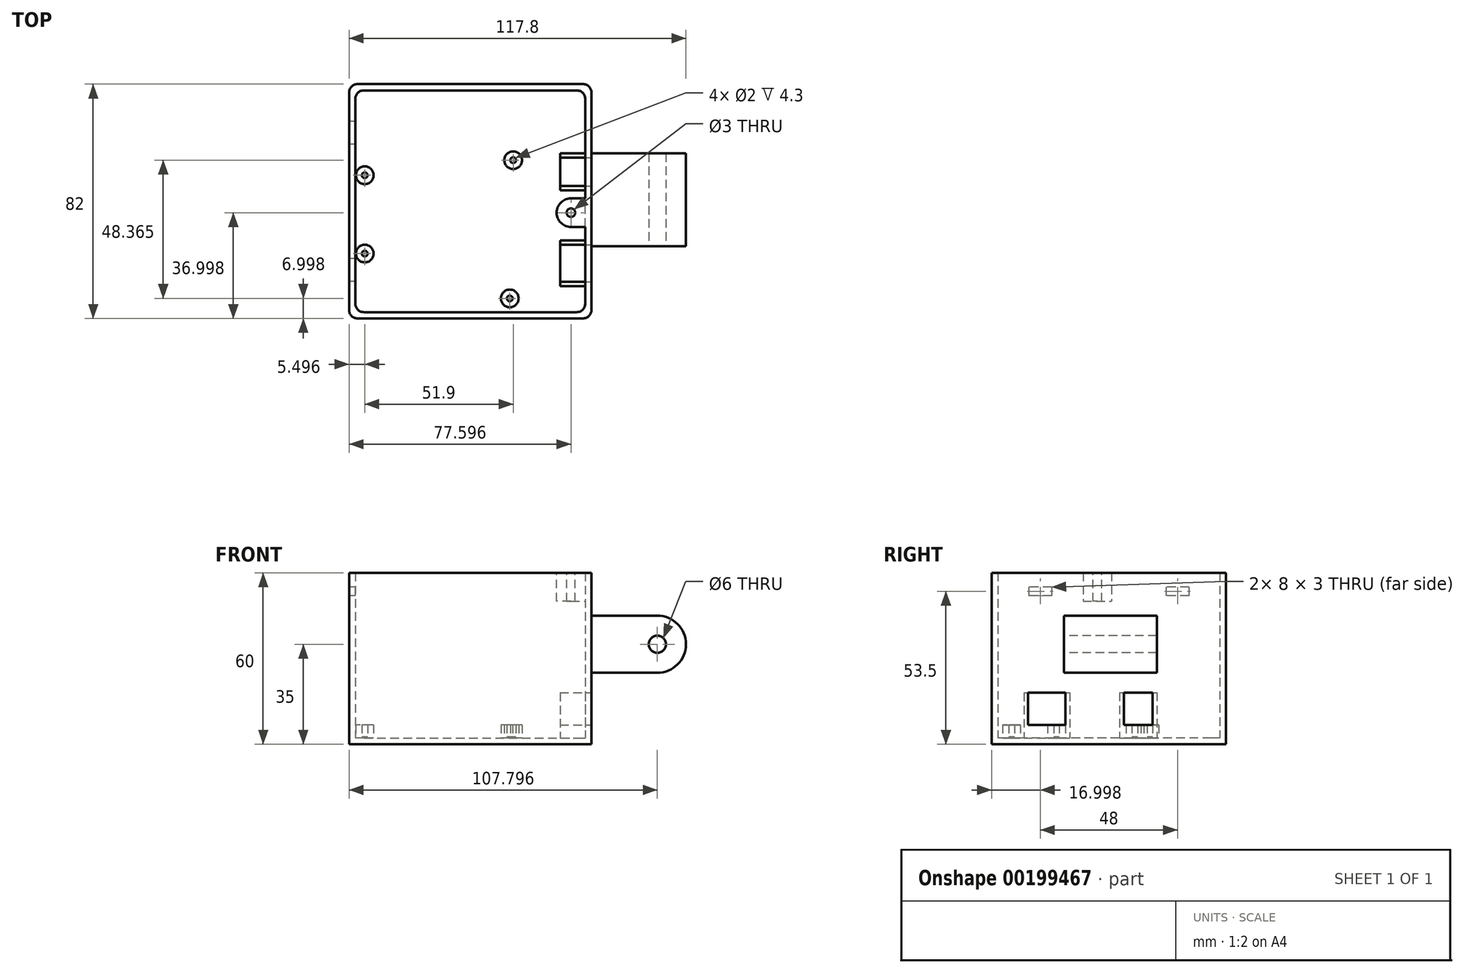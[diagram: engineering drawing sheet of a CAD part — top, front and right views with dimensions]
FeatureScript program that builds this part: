
annotation { "Feature Type Name" : "Feature", "Feature Type Description" : "" }
export const myFeature = defineFeature(function(context is Context, id is Id, definition is map)
    precondition{}
    {
        {
            var Q0;
            Q0=qCreatedBy(makeId("Top.planeOp"),FACE);
            var sketch = newSketch(context, id + "F0", { "sketchPlane" : qUnion([Q0])});
            skLineSegment(sketch, "E0.bottom", {"start": v(-75.5, 40.49) * mm, "end": v(9.3, 40.49) * mm});
            skLineSegment(sketch, "E0.top", {"start": v(-75.5, -41.51) * mm, "end": v(9.3, -41.51) * mm});
            skLineSegment(sketch, "E0.left", {"start": v(-75.5, 40.49) * mm, "end": v(-75.5, -41.51) * mm});
            skLineSegment(sketch, "E0.right", {"start": v(9.3, 40.49) * mm, "end": v(9.3, -41.51) * mm});
            skCircle(sketch, "E1", {"center": v(-70, 8.59) * mm, "radius": 3.1 * mm});
            skCircle(sketch, "E2", {"center": v(-70, -18.81) * mm, "radius": 3.1 * mm});
            skCircle(sketch, "E3", {"center": v(-19.3, -34.51) * mm, "radius": 3.1 * mm});
            skCircle(sketch, "E4", {"center": v(-18.1, 13.85) * mm, "radius": 3.1 * mm});
            skCircle(sketch, "E5", {"center": v(-70, 8.59) * mm, "radius": 1 * mm});
            skCircle(sketch, "E6", {"center": v(-18.1, 13.85) * mm, "radius": 1 * mm});
            skCircle(sketch, "E7", {"center": v(-70, -18.81) * mm, "radius": 1 * mm});
            skCircle(sketch, "E8", {"center": v(-19.3, -34.51) * mm, "radius": 1 * mm});
            skSolve(sketch);
        }
        {
            var Q0;
            Q0=makeQuery(id+"F0.imprint","IMPRINT",FACE,{"disambiguationData":[TD([[makeQuery(id+"F0.imprint","IMPRINT",EDGE,{"derivedFrom":sQuery(id+"F0.wireOp",EDGE,"E0.bottom")}),-1.0]])]});
            var Q1;
            Q1=makeQuery(id+"F0.imprint","IMPRINT",FACE,{"disambiguationData":[TD([[makeQuery(id+"F0.imprint","IMPRINT",EDGE,{"derivedFrom":sQuery(id+"F0.wireOp",EDGE,"E2")}),1.0]])]});
            var Q2;
            Q2=makeQuery(id+"F0.imprint","IMPRINT",FACE,{"disambiguationData":[TD([[makeQuery(id+"F0.imprint","IMPRINT",EDGE,{"derivedFrom":sQuery(id+"F0.wireOp",EDGE,"E1")}),1.0]])]});
            var Q3;
            Q3=makeQuery(id+"F0.imprint","IMPRINT",FACE,{"disambiguationData":[TD([[makeQuery(id+"F0.imprint","IMPRINT",EDGE,{"derivedFrom":sQuery(id+"F0.wireOp",EDGE,"E4")}),1.0]])]});
            var Q4;
            Q4=makeQuery(id+"F0.imprint","IMPRINT",FACE,{"disambiguationData":[TD([[makeQuery(id+"F0.imprint","IMPRINT",EDGE,{"derivedFrom":sQuery(id+"F0.wireOp",EDGE,"E3")}),1.0]])]});
            extrude(context, id + "F1", {"entities" : qUnion([Q0, Q1, Q2, Q3, Q4]), "depth" : 60 * mm});
        }
        {
            var Q0;
            Q0=makeQuery(id+"F1.opExtrude","SWEPT_FACE",FACE,{"disambiguationData":[OSD([sQuery(id+"F0.wireOp",EDGE,"E2")])]});
            var Q1;
            Q1=makeQuery(id+"F1.opExtrude","SWEPT_FACE",FACE,{"disambiguationData":[OSD([sQuery(id+"F0.wireOp",EDGE,"E1")])]});
            var Q2;
            Q2=makeQuery(id+"F1.opExtrude","SWEPT_FACE",FACE,{"disambiguationData":[OSD([sQuery(id+"F0.wireOp",EDGE,"E4")])]});
            var Q3;
            Q3=makeQuery(id+"F1.opExtrude","SWEPT_FACE",FACE,{"disambiguationData":[OSD([sQuery(id+"F0.wireOp",EDGE,"E3")])]});
            var Q4;
            Q4=makeQuery(id+"F1.opExtrude","SWEPT_FACE",FACE,{"disambiguationData":[OSD([sQuery(id+"F0.wireOp",EDGE,"E7")])]});
            var Q5;
            Q5=makeQuery(id+"F1.opExtrude","SWEPT_FACE",FACE,{"disambiguationData":[OSD([sQuery(id+"F0.wireOp",EDGE,"E5")])]});
            var Q6;
            Q6=makeQuery(id+"F1.opExtrude","SWEPT_FACE",FACE,{"disambiguationData":[OSD([sQuery(id+"F0.wireOp",EDGE,"E8")])]});
            var Q7;
            Q7=makeQuery(id+"F1.opExtrude","SWEPT_FACE",FACE,{"disambiguationData":[OSD([sQuery(id+"F0.wireOp",EDGE,"E6")])]});
            var Q8;
            Q8=makeQuery(id+"F1.opExtrude","CAP_FACE",FACE,{"disambiguationData":[OSD([sQuery(id+"F0.wireOp",EDGE,"E0.bottom"),sQuery(id+"F0.wireOp",EDGE,"E0.left"),sQuery(id+"F0.wireOp",EDGE,"7W9O8lOB-wSMZ-6HX8-2Pzd-baJFNFpb0Sld")])],"isStart":false});
            var Q9;
            Q9=makeQuery(id+"F1.opExtrude","CAP_FACE",FACE,{"disambiguationData":[OSD([sQuery(id+"F0.wireOp",EDGE,"E0.bottom"),sQuery(id+"F0.wireOp",EDGE,"E0.right"),sQuery(id+"F0.wireOp",EDGE,"6wA7PAN0-a5WZ-xzTv-JZU7-1fsM9sgV2JZ6")])],"isStart":false});
            var Q10;
            Q10=makeQuery(id+"F1.opExtrude","SWEPT_FACE",FACE,{"disambiguationData":[OSD([sQuery(id+"F0.wireOp",EDGE,"u36fmcnV-SRn1-kItR-ujeD-uHerwh8gpMvl")])]});
            shell(context, id + "F2", {"entities" : qUnion([Q0, Q1, Q2, Q3, Q4, Q5, Q6, Q7, Q8, Q9, Q10]), "thickness" : 2.2 * mm});
        }
        {
            var Q0;
            Q0=makeQuery(id+"F1.opExtrude","SWEPT_FACE",FACE,{"disambiguationData":[OSD([sQuery(id+"F0.wireOp",EDGE,"E0.right")])]});
            var sketch = newSketch(context, id + "F3", { "sketchPlane" : qUnion([Q0])});
            skLineSegment(sketch, "E9.bottom", {"start": v(-28.71, 18.1) * mm, "end": v(-15.71, 18.1) * mm});
            skLineSegment(sketch, "E9.top", {"start": v(-28.71, 6.8) * mm, "end": v(-15.71, 6.8) * mm});
            skLineSegment(sketch, "E9.left", {"start": v(-28.71, 18.1) * mm, "end": v(-28.71, 6.8) * mm});
            skLineSegment(sketch, "E9.right", {"start": v(-15.71, 18.1) * mm, "end": v(-15.71, 6.8) * mm});
            skLineSegment(sketch, "E10.bottom", {"start": v(4.79, 18.1) * mm, "end": v(14.79, 18.1) * mm});
            skLineSegment(sketch, "E10.top", {"start": v(4.79, 6.8) * mm, "end": v(14.79, 6.8) * mm});
            skLineSegment(sketch, "E10.left", {"start": v(4.79, 18.1) * mm, "end": v(4.79, 6.8) * mm});
            skLineSegment(sketch, "E10.right", {"start": v(14.79, 18.1) * mm, "end": v(14.79, 6.8) * mm});
            skLineSegment(sketch, "E11.bottom", {"start": v(-30.21, 18.04) * mm, "end": v(-14.21, 18.04) * mm});
            skLineSegment(sketch, "E11.top", {"start": v(-30.21, 0) * mm, "end": v(-14.21, 0) * mm});
            skLineSegment(sketch, "E11.left", {"start": v(-30.21, 18.04) * mm, "end": v(-30.21, 0) * mm});
            skLineSegment(sketch, "E11.right", {"start": v(-14.21, 18.04) * mm, "end": v(-14.21, 0) * mm});
            skLineSegment(sketch, "E12.bottom", {"start": v(3.29, 18.1) * mm, "end": v(16.29, 18.1) * mm});
            skLineSegment(sketch, "E12.top", {"start": v(3.29, 0) * mm, "end": v(16.29, 0) * mm});
            skLineSegment(sketch, "E12.left", {"start": v(3.29, 18.1) * mm, "end": v(3.29, 0) * mm});
            skLineSegment(sketch, "E12.right", {"start": v(16.29, 18.1) * mm, "end": v(16.29, 0) * mm});
            skSolve(sketch);
        }
        {
            var Q0;
            {var subQ1=sQuery(id+"F3.wireOp",EDGE,"E9.top");Q0=makeQuery(id+"F3.imprint","IMPRINT",FACE,{"disambiguationData":[TD([[makeQuery(id+"F3.imprint","IMPRINT",EDGE,{"derivedFrom":subQ1}),-1.0]])]});}
            var Q1;
            Q1=makeQuery(id+"F3.imprint","IMPRINT",FACE,{"disambiguationData":[TD([[makeQuery(id+"F3.imprint","IMPRINT",EDGE,{"derivedFrom":sQuery(id+"F3.wireOp",EDGE,"E10.top")}),-1.0]])]});
            extrude(context, id + "F4", {"entities" : qUnion([Q0, Q1]), "operationType" : NewBodyOperationType.ADD, "oppositeDirection" : true, "depth" : 11 * mm});
        }
        {
            var Q0;
            {var subQ0=sQuery(id+"F3.wireOp",EDGE,"E9.top");Q0=makeQuery(id+"F3.imprint","IMPRINT",FACE,{"disambiguationData":[TD([[makeQuery(id+"F3.imprint","IMPRINT",EDGE,{"derivedFrom":subQ0}),1.0]])]});}
            extrude(context, id + "F5", {"entities" : qUnion([Q0]), "operationType" : NewBodyOperationType.REMOVE, "oppositeDirection" : true, "depth" : 12 * mm});
        }
        {
            var Q0;
            Q0=makeQuery(id+"F3.imprint","IMPRINT",FACE,{"disambiguationData":[TD([[makeQuery(id+"F3.imprint","IMPRINT",EDGE,{"derivedFrom":sQuery(id+"F3.wireOp",EDGE,"E10.top")}),1.0]])]});
            extrude(context, id + "F6", {"entities" : qUnion([Q0]), "operationType" : NewBodyOperationType.REMOVE, "oppositeDirection" : true, "depth" : 25 * mm});
        }
        {
            var Q0;
            Q0=makeQuery(id+"F1.opExtrude","SWEPT_EDGE",EDGE,{"disambiguationData":[OSD([sQuery(id+"F0.wireOp",EDGE,"E0.top"),sQuery(id+"F0.wireOp",EDGE,"E0.right")])]});
            var Q1;
            Q1=makeQuery(id+"F1.opExtrude","SWEPT_EDGE",EDGE,{"disambiguationData":[OSD([sQuery(id+"F0.wireOp",EDGE,"E0.bottom"),sQuery(id+"F0.wireOp",EDGE,"E0.right")])]});
            var Q2;
            Q2=makeQuery(id+"F1.opExtrude","SWEPT_EDGE",EDGE,{"disambiguationData":[OSD([sQuery(id+"F0.wireOp",EDGE,"E0.bottom"),sQuery(id+"F0.wireOp",EDGE,"E0.left")])]});
            var Q3;
            Q3=makeQuery(id+"F1.opExtrude","SWEPT_EDGE",EDGE,{"disambiguationData":[OSD([sQuery(id+"F0.wireOp",EDGE,"E0.top"),sQuery(id+"F0.wireOp",EDGE,"E0.left")])]});
            var Q4;
            Q4=makeQuery(id+"F2.opShell","OFFSET_EDGE",EDGE,{"disambiguationData":[OSD([sQuery(id+"F0.wireOp",EDGE,"E0.bottom"),sQuery(id+"F0.wireOp",EDGE,"E0.right")])]});
            var Q5;
            Q5=makeQuery(id+"F2.opShell","OFFSET_EDGE",EDGE,{"disambiguationData":[OSD([sQuery(id+"F0.wireOp",EDGE,"E0.top"),sQuery(id+"F0.wireOp",EDGE,"E0.right")])]});
            var Q6;
            Q6=makeQuery(id+"F2.opShell","OFFSET_EDGE",EDGE,{"disambiguationData":[OSD([sQuery(id+"F0.wireOp",EDGE,"E0.top"),sQuery(id+"F0.wireOp",EDGE,"E0.left")])]});
            var Q7;
            Q7=makeQuery(id+"F2.opShell","OFFSET_EDGE",EDGE,{"disambiguationData":[OSD([sQuery(id+"F0.wireOp",EDGE,"E0.bottom"),sQuery(id+"F0.wireOp",EDGE,"E0.left")])]});
            fillet(context, id + "F7", {"entities" : qUnion([Q0, Q1, Q2, Q3, Q4, Q5, Q6, Q7]), "radius" : 3 * mm, "tangentPropagation" : true, "allowEdgeOverflow" : false});
        }
        {
            var Q0;
            Q0=qCreatedBy(makeId("Front.planeOp"),FACE);
            var sketch = newSketch(context, id + "F8", { "sketchPlane" : qUnion([Q0])});
            skLineSegment(sketch, "E13.bottom", {"start": v(9.3, 45) * mm, "end": v(32.3, 45) * mm});
            skLineSegment(sketch, "E13.top", {"start": v(9.3, 25) * mm, "end": v(32.3, 25) * mm});
            skLineSegment(sketch, "E13.left", {"start": v(9.3, 45) * mm, "end": v(9.3, 25) * mm});
            skLineSegment(sketch, "E13.right", {"start": v(32.3, 45) * mm, "end": v(32.3, 25) * mm});
            skCircle(sketch, "E14", {"center": v(32.3, 35) * mm, "radius": 10 * mm});
            skCircle(sketch, "E15", {"center": v(32.3, 35) * mm, "radius": 3 * mm});
            skSolve(sketch);
        }
        {
            var Q0;
            {var subQ0=sQuery(id+"F8.wireOp",EDGE,"E13.bottom");Q0=makeQuery(id+"F8.imprint","IMPRINT",FACE,{"disambiguationData":[TD([[makeQuery(id+"F8.imprint","IMPRINT",EDGE,{"derivedFrom":subQ0}),-1.0]])]});}
            var Q1;
            {var subQ0=sQuery(id+"F8.wireOp",EDGE,"E15");var subQ1=sQuery(id+"F8.wireOp",EDGE,"E13.right");var subQ2=makeQuery(id+"F8.imprint","INTERSECT",VERTEX,{"disambiguationData":[OD(0.0)],"derivedFrom":[subQ1,subQ0]});Q1=makeQuery(id+"F8.imprint","IMPRINT",FACE,{"disambiguationData":[TD([[makeQuery(id+"F8.imprint","IMPRINT",EDGE,{"disambiguationData":[TD([[subQ2,-1.0]])],"derivedFrom":subQ1}),1.0]])]});}
            var Q2;
            {var subQ1=sQuery(id+"F8.wireOp",EDGE,"E13.right");var subQ3=sQuery(id+"F8.wireOp",EDGE,"E15");var subQ4=makeQuery(id+"F8.imprint","INTERSECT",VERTEX,{"disambiguationData":[OD(0.0)],"derivedFrom":[subQ1,subQ3]});Q2=makeQuery(id+"F8.imprint","IMPRINT",FACE,{"disambiguationData":[TD([[makeQuery(id+"F8.imprint","IMPRINT",EDGE,{"disambiguationData":[TD([[subQ4,1.0]])],"derivedFrom":subQ3}),-1.0]])]});}
            var Q3;
            {var subQ1=sQuery(id+"F8.wireOp",EDGE,"E13.right");var subQ3=sQuery(id+"F8.wireOp",EDGE,"E15");var subQ4=makeQuery(id+"F8.imprint","INTERSECT",VERTEX,{"disambiguationData":[OD(0.0)],"derivedFrom":[subQ1,subQ3]});Q3=makeQuery(id+"F8.imprint","IMPRINT",FACE,{"disambiguationData":[TD([[makeQuery(id+"F8.imprint","IMPRINT",EDGE,{"disambiguationData":[TD([[subQ4,-1.0]])],"derivedFrom":subQ3}),-1.0]])]});}
            var Q4;
            {var subQ0=sQuery(id+"F8.wireOp",EDGE,"E15");var subQ1=sQuery(id+"F8.wireOp",EDGE,"E13.right");var subQ2=makeQuery(id+"F8.imprint","INTERSECT",VERTEX,{"disambiguationData":[OD(0.0)],"derivedFrom":[subQ1,subQ0]});Q4=makeQuery(id+"F8.imprint","IMPRINT",FACE,{"disambiguationData":[TD([[makeQuery(id+"F8.imprint","IMPRINT",EDGE,{"disambiguationData":[TD([[subQ2,-1.0]])],"derivedFrom":subQ1}),-1.0]])]});}
            extrude(context, id + "F9", {"entities" : qUnion([Q0, Q1, Q2, Q3, Q4]), "operationType" : NewBodyOperationType.ADD, "depth" : 16.25 * mm, "hasSecondDirection" : true, "secondDirectionOppositeDirection" : true, "secondDirectionDepth" : 16.25 * mm});
        }
        {
            var Q0;
            {var subQ0=sQuery(id+"F8.wireOp",EDGE,"E15");var subQ1=sQuery(id+"F8.wireOp",EDGE,"E13.right");var subQ2=makeQuery(id+"F8.imprint","INTERSECT",VERTEX,{"disambiguationData":[OD(0.0)],"derivedFrom":[subQ1,subQ0]});Q0=makeQuery(id+"F8.imprint","IMPRINT",FACE,{"disambiguationData":[TD([[makeQuery(id+"F8.imprint","IMPRINT",EDGE,{"disambiguationData":[TD([[subQ2,-1.0]])],"derivedFrom":subQ1}),1.0]])]});}
            var Q1;
            {var subQ0=sQuery(id+"F8.wireOp",EDGE,"E15");var subQ1=sQuery(id+"F8.wireOp",EDGE,"E13.right");var subQ2=makeQuery(id+"F8.imprint","INTERSECT",VERTEX,{"disambiguationData":[OD(0.0)],"derivedFrom":[subQ1,subQ0]});Q1=makeQuery(id+"F8.imprint","IMPRINT",FACE,{"disambiguationData":[TD([[makeQuery(id+"F8.imprint","IMPRINT",EDGE,{"disambiguationData":[TD([[subQ2,-1.0]])],"derivedFrom":subQ1}),-1.0]])]});}
            extrude(context, id + "F10", {"entities" : qUnion([Q0, Q1]), "operationType" : NewBodyOperationType.REMOVE, "oppositeDirection" : true, "depth" : 25 * mm, "hasSecondDirection" : true, "secondDirectionOppositeDirection" : false, "secondDirectionDepth" : 25 * mm});
        }
        {
            var Q0;
            Q0=makeQuery(id+"F1.opExtrude","SWEPT_FACE",FACE,{"disambiguationData":[OSD([sQuery(id+"F0.wireOp",EDGE,"E0.left")])]});
            var sketch = newSketch(context, id + "F11", { "sketchPlane" : qUnion([Q0])});
            skLineSegment(sketch, "E16.bottom", {"start": v(-27.49, 55) * mm, "end": v(-19.49, 55) * mm});
            skLineSegment(sketch, "E16.top", {"start": v(-27.49, 52) * mm, "end": v(-19.49, 52) * mm});
            skLineSegment(sketch, "E16.left", {"start": v(-27.49, 55) * mm, "end": v(-27.49, 52) * mm});
            skLineSegment(sketch, "E16.right", {"start": v(-19.49, 55) * mm, "end": v(-19.49, 52) * mm});
            skLineSegment(sketch, "E17.bottom", {"start": v(20.51, 55) * mm, "end": v(28.51, 55) * mm});
            skLineSegment(sketch, "E17.top", {"start": v(20.51, 52) * mm, "end": v(28.51, 52) * mm});
            skLineSegment(sketch, "E17.left", {"start": v(20.51, 55) * mm, "end": v(20.51, 52) * mm});
            skLineSegment(sketch, "E17.right", {"start": v(28.51, 55) * mm, "end": v(28.51, 52) * mm});
            skSolve(sketch);
        }
        {
            var Q0;
            Q0 = qSketchRegion(id + "F11", true);
            var Q1;
            Q1=makeQuery(id+"F1.opExtrude","SWEPT_FACE",FACE,{"disambiguationData":[OSD([sQuery(id+"F0.wireOp",EDGE,"E0.right")])]});
            extrude(context, id + "F12", {"entities" : qUnion([Q0, Q1]), "operationType" : NewBodyOperationType.REMOVE, "oppositeDirection" : true, "depth" : 2.8 * mm});
        }
        {
            var Q0;
            Q0=makeQuery(id+"F1.opExtrude","SWEPT_FACE",FACE,{"disambiguationData":[OSD([sQuery(id+"F0.wireOp",EDGE,"E0.right")])]});
            var sketch = newSketch(context, id + "F13", { "sketchPlane" : qUnion([Q0])});
            skLineSegment(sketch, "E18.bottom", {"start": v(-9.51, 60) * mm, "end": v(0.49, 60) * mm});
            skLineSegment(sketch, "E18.top", {"start": v(-9.51, 50) * mm, "end": v(0.49, 50) * mm});
            skLineSegment(sketch, "E18.left", {"start": v(-9.51, 60) * mm, "end": v(-9.51, 50) * mm});
            skLineSegment(sketch, "E18.right", {"start": v(0.49, 60) * mm, "end": v(0.49, 50) * mm});
            skSolve(sketch);
        }
        {
            var Q0;
            Q0 = qSketchRegion(id + "F13", true);
            extrude(context, id + "F14", {"entities" : qUnion([Q0]), "operationType" : NewBodyOperationType.ADD, "oppositeDirection" : true, "depth" : 12.2 * mm});
        }
        {
            var Q0;
            Q0=makeQuery(id+"F14.opExtrude","CAP_EDGE",EDGE,{"disambiguationData":[OSD([sQuery(id+"F13.wireOp",EDGE,"E18.left")])],"isStart":false});
            var Q1;
            Q1=makeQuery(id+"F14.opExtrude","CAP_EDGE",EDGE,{"disambiguationData":[OSD([sQuery(id+"F13.wireOp",EDGE,"E18.right")])],"isStart":false});
            fillet(context, id + "F15", {"entities" : qUnion([Q0, Q1]), "radius" : 5 * mm, "tangentPropagation" : true, "allowEdgeOverflow" : false});
        }
        {
            var Q0;
            Q0=makeQuery(id+"F14.boolean.opBoolean","MERGE",FACE,{"derivedFrom":[makeQuery(id+"F1.opExtrude","CAP_FACE",FACE,{"disambiguationData":[OSD([sQuery(id+"F0.wireOp",EDGE,"E0.bottom"),sQuery(id+"F0.wireOp",EDGE,"E0.top"),sQuery(id+"F0.wireOp",EDGE,"E0.left"),sQuery(id+"F0.wireOp",EDGE,"E0.right"),sQuery(id+"F0.wireOp",EDGE,"E5"),sQuery(id+"F0.wireOp",EDGE,"E6"),sQuery(id+"F0.wireOp",EDGE,"E7"),sQuery(id+"F0.wireOp",EDGE,"E8")])],"isStart":false}),makeQuery(id+"F14.opExtrude","SWEPT_FACE",FACE,{"disambiguationData":[OSD([sQuery(id+"F13.wireOp",EDGE,"E18.bottom")])]})]});
            var sketch = newSketch(context, id + "F16", { "sketchPlane" : qUnion([Q0])});
            skCircle(sketch, "E19", {"center": v(2.1, -4.51) * mm, "radius": 1.5 * mm});
            skSolve(sketch);
        }
        {
            var Q0;
            Q0=makeQuery(id+"F16.imprint","IMPRINT",FACE,{"disambiguationData":[TD([[makeQuery(id+"F16.imprint","IMPRINT",EDGE,{"derivedFrom":sQuery(id+"F16.wireOp",EDGE,"E19")}),1.0]])]});
            extrude(context, id + "F17", {"entities" : qUnion([Q0]), "operationType" : NewBodyOperationType.REMOVE, "oppositeDirection" : true, "depth" : 11.6 * mm});
        }
        {
            var Q0;
            Q0=makeQuery(id+"F0.imprint","IMPRINT",FACE,{"disambiguationData":[TD([[makeQuery(id+"F0.imprint","IMPRINT",EDGE,{"derivedFrom":sQuery(id+"F0.wireOp",EDGE,"E1")}),1.0]])]});
            var Q1;
            Q1=makeQuery(id+"F0.imprint","IMPRINT",FACE,{"disambiguationData":[TD([[makeQuery(id+"F0.imprint","IMPRINT",EDGE,{"derivedFrom":sQuery(id+"F0.wireOp",EDGE,"E4")}),1.0]])]});
            var Q2;
            Q2=makeQuery(id+"F0.imprint","IMPRINT",FACE,{"disambiguationData":[TD([[makeQuery(id+"F0.imprint","IMPRINT",EDGE,{"derivedFrom":sQuery(id+"F0.wireOp",EDGE,"E2")}),1.0]])]});
            var Q3;
            Q3=makeQuery(id+"F0.imprint","IMPRINT",FACE,{"disambiguationData":[TD([[makeQuery(id+"F0.imprint","IMPRINT",EDGE,{"derivedFrom":sQuery(id+"F0.wireOp",EDGE,"E3")}),1.0]])]});
            var Q4;
            Q4=sQuery(id+"F0.wireOp",EDGE,"E4");
            var Q5;
            Q5=sQuery(id+"F0.wireOp",EDGE,"E3");
            var Q6;
            Q6=sQuery(id+"F0.wireOp",EDGE,"E1");
            var Q7;
            Q7=sQuery(id+"F0.wireOp",EDGE,"E2");
            extrude(context, id + "F18", {"entities" : qUnion([Q0, Q1, Q2, Q3]), "operationType" : NewBodyOperationType.ADD, "surfaceEntities" : qUnion([Q4, Q5, Q6, Q7]), "depth" : 6.8 * mm});
        }
        {
            var Q0;
            Q0=makeQuery(id+"F0.imprint","IMPRINT",FACE,{"disambiguationData":[TD([[makeQuery(id+"F0.imprint","IMPRINT",EDGE,{"derivedFrom":sQuery(id+"F0.wireOp",EDGE,"E6")}),1.0]])]});
            var Q1;
            Q1=makeQuery(id+"F0.imprint","IMPRINT",FACE,{"disambiguationData":[TD([[makeQuery(id+"F0.imprint","IMPRINT",EDGE,{"derivedFrom":sQuery(id+"F0.wireOp",EDGE,"E1")}),1.0]])]});
            var Q2;
            Q2=makeQuery(id+"F0.imprint","IMPRINT",FACE,{"disambiguationData":[TD([[makeQuery(id+"F0.imprint","IMPRINT",EDGE,{"derivedFrom":sQuery(id+"F0.wireOp",EDGE,"E7")}),1.0]])]});
            var Q3;
            Q3=makeQuery(id+"F0.imprint","IMPRINT",FACE,{"disambiguationData":[TD([[makeQuery(id+"F0.imprint","IMPRINT",EDGE,{"derivedFrom":sQuery(id+"F0.wireOp",EDGE,"E8")}),1.0]])]});
            var Q4;
            Q4=makeQuery(id+"F0.imprint","IMPRINT",FACE,{"disambiguationData":[TD([[makeQuery(id+"F0.imprint","IMPRINT",EDGE,{"derivedFrom":sQuery(id+"F0.wireOp",EDGE,"E5")}),1.0]])]});
            extrude(context, id + "F19", {"entities" : qUnion([Q0, Q1, Q2, Q3, Q4]), "operationType" : NewBodyOperationType.ADD, "depth" : 2.5 * mm});
        }
    });
